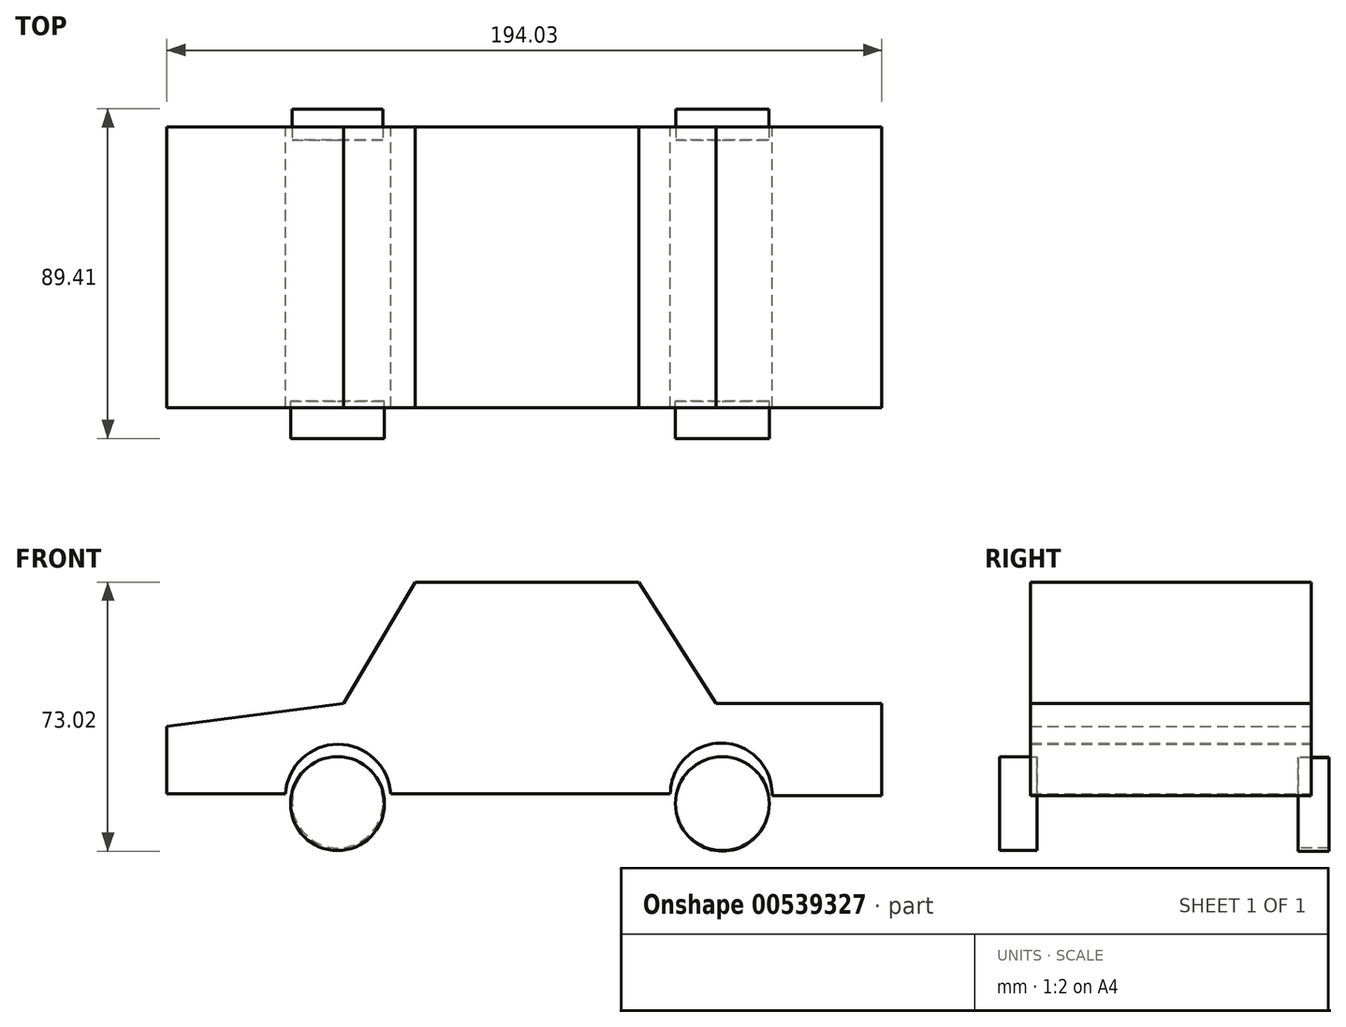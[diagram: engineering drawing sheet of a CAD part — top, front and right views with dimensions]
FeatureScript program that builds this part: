
annotation { "Feature Type Name" : "Feature", "Feature Type Description" : "" }
export const myFeature = defineFeature(function(context is Context, id is Id, definition is map)
    precondition{}
    {
        {
            var Q0;
            Q0=qCreatedBy(makeId("Front.planeOp"),FACE);
            var sketch = newSketch(context, id + "F0", { "sketchPlane" : qUnion([Q0])});
            skLineSegment(sketch, "E0", {"start": v(-46.76, 0) * mm, "end": v(-27.33, 32.95) * mm});
            skLineSegment(sketch, "E1", {"start": v(-27.33, 32.95) * mm, "end": v(33.4, 32.95) * mm});
            skLineSegment(sketch, "E2", {"start": v(33.4, 32.95) * mm, "end": v(54.35, 0) * mm});
            skLineSegment(sketch, "E3", {"start": v(54.35, 0) * mm, "end": v(99.3, 0) * mm});
            skLineSegment(sketch, "E4", {"start": v(99.3, 0) * mm, "end": v(99.3, -25.05) * mm});
            skLineSegment(sketch, "E5", {"start": v(99.3, -25.05) * mm, "end": v(69.53, -25.05) * mm});
            skLineSegment(sketch, "E6", {"start": v(-46.76, 0) * mm, "end": v(-94.74, -6.22) * mm});
            skLineSegment(sketch, "E7", {"start": v(-94.74, -6.22) * mm, "end": v(-94.74, -24.44) * mm});
            skLineSegment(sketch, "E8", {"start": v(-94.74, -24.44) * mm, "end": v(-62.55, -24.44) * mm});
            skLineSegment(sketch, "E9", {"start": v(-34, -24.44) * mm, "end": v(41.9, -24.44) * mm});
            skArc(sketch, "E10", {"start": v(-34, -24.44) * mm, "mid": v(-48.28, -11.08) * mm, "end": v(-62.55, -24.44) * mm});
            skArc(sketch, "E11", {"start": v(69.53, -25.05) * mm, "mid": v(56.03, -10.78) * mm, "end": v(41.9, -24.44) * mm});
            skSolve(sketch);
        }
        {
            var Q0;
            Q0=makeQuery(id+"F0.imprint","IMPRINT",FACE,{"disambiguationData":[TD([[makeQuery(id+"F0.imprint","IMPRINT",EDGE,{"derivedFrom":sQuery(id+"F0.wireOp",EDGE,"E0")}),-1.0]])]});
            extrude(context, id + "F1", {"entities" : qUnion([Q0]), "depth" : 38.1 * mm, "offsetDistance" : 25.4 * mm, "hasSecondDirection" : true, "secondDirectionOppositeDirection" : true, "secondDirectionDepth" : 38.1 * mm});
        }
        {
            var Q0;
            Q0=qCreatedBy(makeId("Front.planeOp"),FACE);
            var sketch = newSketch(context, id + "F2", { "sketchPlane" : qUnion([Q0])});
            skCircle(sketch, "E12", {"center": v(-48.43, -27.18) * mm, "radius": 12.76 * mm});
            skCircle(sketch, "E13", {"center": v(56.02, -27.18) * mm, "radius": 12.75 * mm});
            skSolve(sketch);
        }
        {
            var Q0;
            Q0=makeQuery(id+"F2.imprint","IMPRINT",FACE,{"disambiguationData":[TD([[makeQuery(id+"F2.imprint","IMPRINT",EDGE,{"derivedFrom":sQuery(id+"F2.wireOp",EDGE,"E12")}),1.0]])]});
            var Q1;
            Q1=makeQuery(id+"F2.imprint","IMPRINT",FACE,{"disambiguationData":[TD([[makeQuery(id+"F2.imprint","IMPRINT",EDGE,{"derivedFrom":sQuery(id+"F2.wireOp",EDGE,"E13")}),1.0]])]});
            extrude(context, id + "F3", {"entities" : qUnion([Q0, Q1]), "depth" : 46.48 * mm, "offsetDistance" : 25.4 * mm, "hasSecondDirection" : true, "secondDirectionOppositeDirection" : false, "secondDirectionDepth" : 36.32 * mm});
        }
        {
            var Q0;
            Q0=qCreatedBy(makeId("Front.planeOp"),FACE);
            var sketch = newSketch(context, id + "F4", { "sketchPlane" : qUnion([Q0])});
            skCircle(sketch, "E14", {"center": v(56.02, -27.4) * mm, "radius": 12.68 * mm});
            skCircle(sketch, "E15", {"center": v(-48.41, -26.88) * mm, "radius": 12.32 * mm});
            skSolve(sketch);
        }
        {
            var Q0;
            Q0 = qSketchRegion(id + "F4", true);
            extrude(context, id + "F5", {"entities" : qUnion([Q0]), "oppositeDirection" : true, "depth" : 42.93 * mm, "offsetDistance" : 25.4 * mm, "hasSecondDirection" : true, "secondDirectionOppositeDirection" : true, "secondDirectionDepth" : 34.54 * mm});
        }
    });
